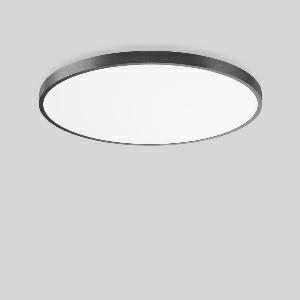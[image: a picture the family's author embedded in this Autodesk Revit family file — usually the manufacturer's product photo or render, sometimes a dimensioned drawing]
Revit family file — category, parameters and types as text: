
# Revit family: triona_round_a_312391_0031_1_76_cfc1
name_source: partatom
category: Lighting Fixtures
units: mm (PartAtom-declared; Revit-internal decimal feet)

## family parameters
Cut with Voids When Loaded = No
Host = Face
Light Source = No
Part Type = Normal
Room Calculation Point = No
Round Connector Dimension = Use Diameter
Shared = No

## types (1)
- TRIONA round A (1 x LED Modul 840, 11700 lm, 4000)
    Apparent Load = 106 VA
    CIE Flux Codes = 49 80 96 100 100
    Color Rendering = 80
    Color Temperature = 4000
    Default Elevation = 1800 mm
    Description = Series: TRIONA round
Decorative round LED surface-mounted luminaire. Flat, seamless frame: aluminium extrusion profile, powder coated. Cover made of sheet steel, powder-coated. Light emission through a diffuser: plastic, opal. Lightguide and diffuser made of non-yellowing plastic (PMMA). Lateral light emission (RZB SIDELITE technology) for above-average homogeneous light distribution. Suitable for Ceiling mounting, Wall (surface). Tool-free mounting via bayonet connection. Electronic ballast included. Very easy installation thanks to Plug+Play connection. 
Colour: anthracite metallic (DB703)
Diameter: 1009 mm
Height: 88 mm
Lamp: LED
Socket: without socket
Colour temperature: 4000K
Colour rendering index (CRI): 80
System power: 106 W
Rated luminous flux: 11700 lm
Luminous efficiency: 110 lm/W
Control gear: Converter, dimmable, DALI
Protection class: I
Type of protection: IP 20
    Height = 88 mm
    Lamp = 1 x LED Modul 840
    Lamp Light Flux = 11700 lm
    Lamp count = 1
    Length = 1009 mm
    Lifetime = 50000 h
    Luminous efficacy = 110 lm/W
    Manufacturer = RZB
    ModVariant = No
    Model = 312391.0031.1.76
    Mounting Place = Ceiling
    Mounting Type = Surface mounted
    Number of Poles = 1
    OnlyDefault = Yes
    Power Factor = 1
    Product Name = TRIONA round A
    Product group = Surface mounted modular luminaires
    ProductGroupID = 306
    Protection Class = Protection class I
    Protection Degree = IP 20
    RLX_Detail_Level = 1
    RLX_Emergency_Light_Flux = 0 lm
    RLX_Emergency_Type = 0
    RLX_Emergency_Type_DB = No
    RlxData = <blob elided: 40381 chars, md5=9c3fb8eb>
    Socket = socket
    Standby Power = 0 W
    System Light Flux = 11700 lm
    System Power = 106 W
    Type Comments = Product without accessories
    Type Image = 312392.0031.jpg
    URL = http://relux.com
    VarID = ---
    Voltage = 230 V
    Voltage Range = 220-240 V
    Weight = 0.00 kg
    Width = 0 mm  [stored 0 ft]

note: [stored X ft] marks values corroborated as IEEE doubles in the binary element streams (Revit-internal decimal feet)

## geometry (parser evidence)
native form markers: Blend x4, Sweep x10
no freeform markers — native parametric forms only
